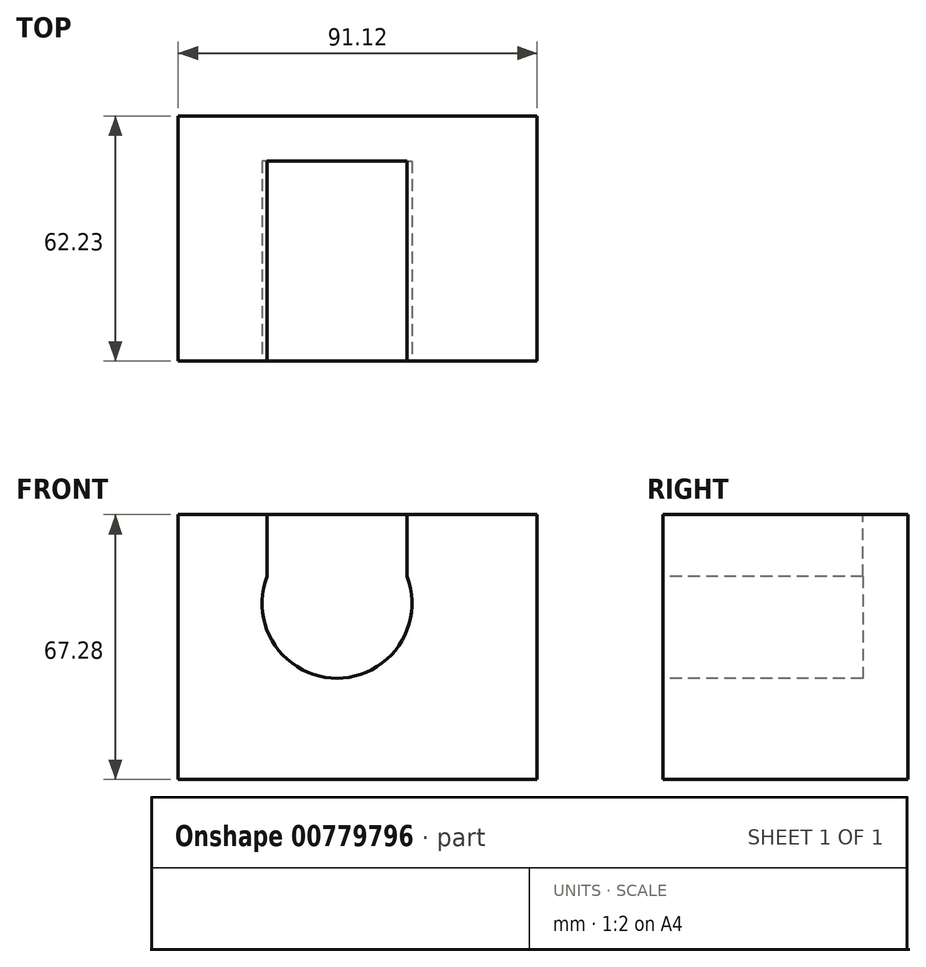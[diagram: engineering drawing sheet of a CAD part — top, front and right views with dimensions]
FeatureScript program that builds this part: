
annotation { "Feature Type Name" : "Feature", "Feature Type Description" : "" }
export const myFeature = defineFeature(function(context is Context, id is Id, definition is map)
    precondition{}
    {
        {
            var Q0;
            Q0=qCreatedBy(makeId("Front.planeOp"),FACE);
            var sketch = newSketch(context, id + "F0", { "sketchPlane" : qUnion([Q0])});
            skLineSegment(sketch, "E0.bottom", {"start": v(-39.85, 26.66) * mm, "end": v(51.27, 26.66) * mm});
            skLineSegment(sketch, "E0.top", {"start": v(-39.85, -40.62) * mm, "end": v(51.27, -40.62) * mm});
            skLineSegment(sketch, "E0.left", {"start": v(-39.85, 26.66) * mm, "end": v(-39.85, -40.62) * mm});
            skLineSegment(sketch, "E0.right", {"start": v(51.27, 26.66) * mm, "end": v(51.27, -40.62) * mm});
            skSolve(sketch);
        }
        {
            var Q0;
            Q0=makeQuery(id+"F0.imprint","IMPRINT",FACE,{"disambiguationData":[TD([[makeQuery(id+"F0.imprint","IMPRINT",EDGE,{"derivedFrom":sQuery(id+"F0.wireOp",EDGE,"E0.bottom")}),-1.0]])]});
            var Q1;
            Q1=sQuery(id+"F0.wireOp",EDGE,"E0.bottom");
            var Q2;
            Q2=sQuery(id+"F0.wireOp",EDGE,"E0.left");
            var Q3;
            Q3=sQuery(id+"F0.wireOp",EDGE,"E0.top");
            var Q4;
            Q4=sQuery(id+"F0.wireOp",EDGE,"E0.right");
            extrude(context, id + "F1", {"entities" : qUnion([Q0]), "surfaceEntities" : qUnion([Q1, Q2, Q3, Q4]), "depth" : 62.23 * mm, "offsetDistance" : 25.4 * mm});
        }
        {
            var Q0;
            Q0=makeQuery(id+"F1.opExtrude","CAP_FACE",FACE,{"disambiguationData":[OSD([sQuery(id+"F0.wireOp",EDGE,"E0.bottom"),sQuery(id+"F0.wireOp",EDGE,"E0.top"),sQuery(id+"F0.wireOp",EDGE,"E0.left"),sQuery(id+"F0.wireOp",EDGE,"E0.right")])],"isStart":false});
            var sketch = newSketch(context, id + "F2", { "sketchPlane" : qUnion([Q0])});
            skCircle(sketch, "E1", {"center": v(0.47, 4.12) * mm, "radius": 19.05 * mm});
            skSolve(sketch);
        }
        {
            var Q0;
            {var subQ0=sQuery(id+"F2.wireOp",EDGE,"E1");var subQ1=makeQuery(id+"F1.opExtrude","CAP_EDGE",EDGE,{"disambiguationData":[OSD([sQuery(id+"F0.wireOp",EDGE,"E0.bottom")])],"isStart":false});var subQ2=makeQuery(id+"F2.imprint","INTERSECT",VERTEX,{"disambiguationData":[OD(0.0)],"derivedFrom":[subQ1,subQ0]});Q0=makeQuery(id+"F2.imprint","IMPRINT",FACE,{"disambiguationData":[TD([[makeQuery(id+"F2.imprint","IMPRINT",EDGE,{"disambiguationData":[TD([[subQ2,-1.0]])],"derivedFrom":subQ0}),1.0]])]});}
            var Q1;
            Q1=sQuery(id+"F2.wireOp",EDGE,"E1");
            extrude(context, id + "F3", {"entities" : qUnion([Q0]), "operationType" : NewBodyOperationType.REMOVE, "surfaceEntities" : qUnion([Q1]), "oppositeDirection" : true, "depth" : 50.8 * mm, "offsetDistance" : 25.4 * mm});
        }
        {
            var Q0;
            Q0=makeQuery(id+"F1.opExtrude","CAP_FACE",FACE,{"disambiguationData":[OSD([sQuery(id+"F0.wireOp",EDGE,"E0.bottom"),sQuery(id+"F0.wireOp",EDGE,"E0.top"),sQuery(id+"F0.wireOp",EDGE,"E0.left"),sQuery(id+"F0.wireOp",EDGE,"E0.right")])],"isStart":false});
            var sketch = newSketch(context, id + "F4", { "sketchPlane" : qUnion([Q0])});
            skLineSegment(sketch, "E2", {"start": v(18.25, 26.66) * mm, "end": v(18.25, -2.71) * mm});
            skLineSegment(sketch, "E3", {"start": v(-17.31, 26.66) * mm, "end": v(-17.31, -2.71) * mm});
            skLineSegment(sketch, "E4", {"start": v(0.47, 4.12) * mm, "end": v(0.47, 43.04) * mm});
            skSolve(sketch);
        }
        {
            var Q0;
            {var subQ0=sQuery(id+"F4.wireOp",EDGE,"E2");Q0=makeQuery(id+"F4.imprint","IMPRINT",FACE,{"disambiguationData":[TD([[makeQuery(id+"F4.imprint","IMPRINT",EDGE,{"derivedFrom":subQ0}),-1.0]])]});}
            var Q1;
            {var subQ0=sQuery(id+"F4.wireOp",EDGE,"E3");Q1=makeQuery(id+"F4.imprint","IMPRINT",FACE,{"disambiguationData":[TD([[makeQuery(id+"F4.imprint","IMPRINT",EDGE,{"derivedFrom":subQ0}),1.0]])]});}
            var Q2;
            Q2=makeQuery(id+"F3.boolean.opBoolean","COPY",FACE,{"derivedFrom":makeQuery(id+"F3.opExtrude","CAP_FACE",FACE,{"disambiguationData":[OSD([sQuery(id+"F0.wireOp",EDGE,"E0.bottom"),sQuery(id+"F2.wireOp",EDGE,"E1")])],"isStart":false})});
            extrude(context, id + "F5", {"entities" : qUnion([Q0, Q1]), "operationType" : NewBodyOperationType.REMOVE, "endBound" : BoundingType.UP_TO_SURFACE, "oppositeDirection" : true, "depth" : 25.4 * mm, "endBoundEntityFace" : qUnion([Q2]), "offsetDistance" : 25.4 * mm});
        }
    });
